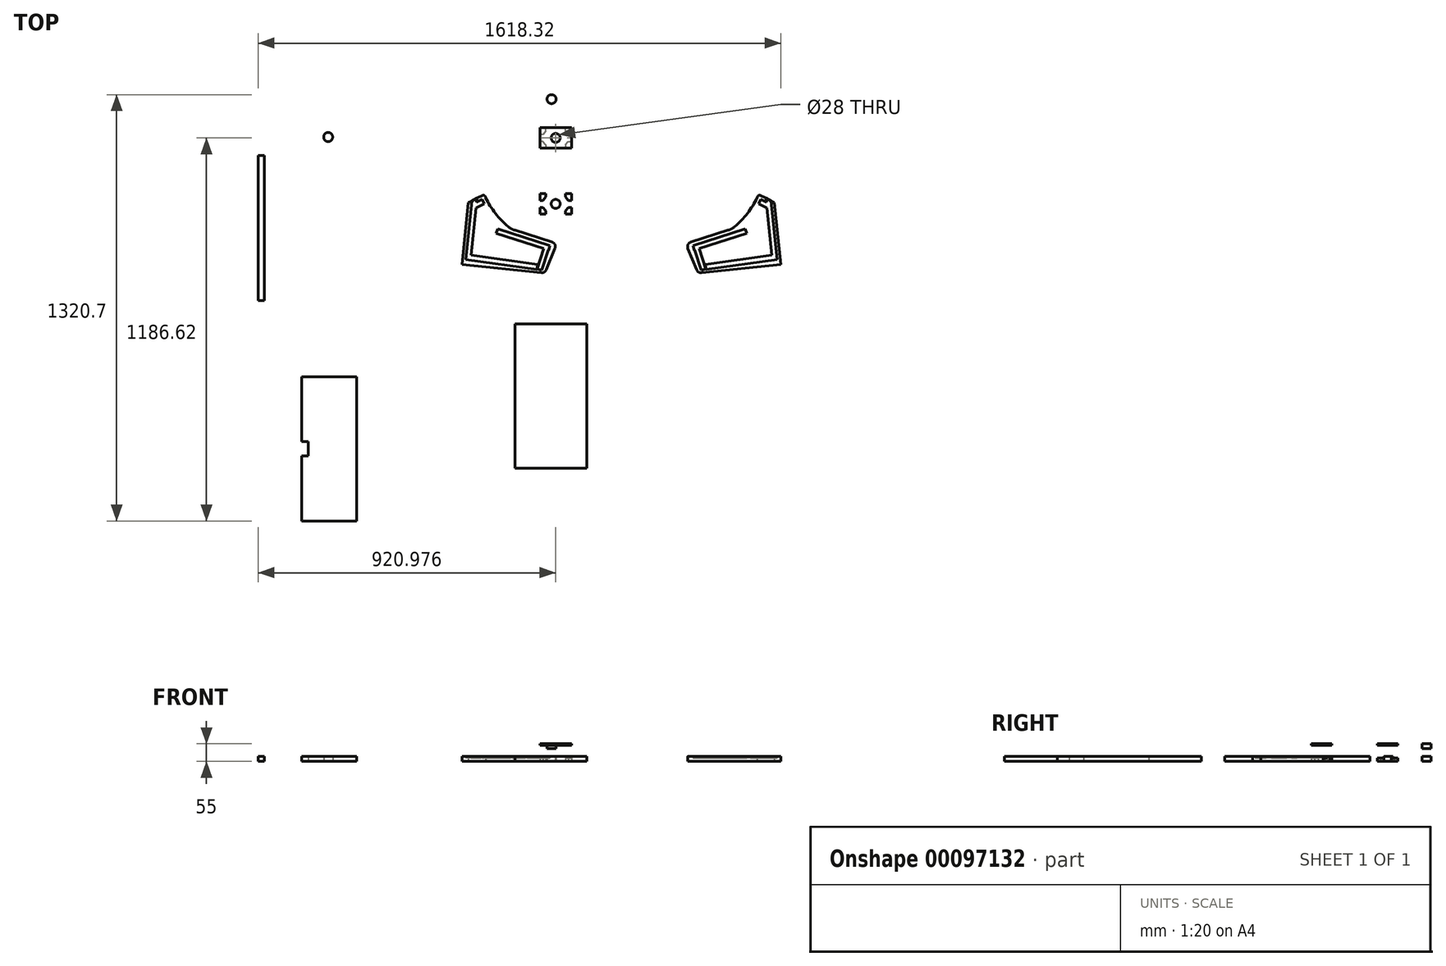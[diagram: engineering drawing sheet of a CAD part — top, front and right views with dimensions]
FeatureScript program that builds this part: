
annotation { "Feature Type Name" : "Feature", "Feature Type Description" : "" }
export const myFeature = defineFeature(function(context is Context, id is Id, definition is map)
    precondition{}
    {
        {
            var Q0;
            Q0=qCreatedBy(makeId("Top.planeOp"),FACE);
            var sketch = newSketch(context, id + "F0", { "sketchPlane" : qUnion([Q0])});
            skCircle(sketch, "E0", {"center": v(416.31, 292.57) * mm, "radius": 14 * mm});
            skCircle(sketch, "E1", {"center": v(380.31, 292.57) * mm, "radius": 14 * mm});
            skCircle(sketch, "E2", {"center": v(389.31, 257.57) * mm, "radius": 14 * mm});
            skCircle(sketch, "E3", {"center": v(425.31, 257.57) * mm, "radius": 14 * mm});
            skCircle(sketch, "E4", {"center": v(407.31, 226.32) * mm, "radius": 14 * mm});
            skCircle(sketch, "E5", {"center": v(443.31, 226.32) * mm, "radius": 14 * mm});
            skCircle(sketch, "E6", {"center": v(416.31, 87.32) * mm, "radius": 14 * mm});
            skCircle(sketch, "E7", {"center": v(380.31, 87.32) * mm, "radius": 14 * mm});
            skCircle(sketch, "E8", {"center": v(389.31, 52.32) * mm, "radius": 14 * mm});
            skCircle(sketch, "E9", {"center": v(425.31, 52.32) * mm, "radius": 14 * mm});
            skCircle(sketch, "E10", {"center": v(407.31, 21.07) * mm, "radius": 14 * mm});
            skCircle(sketch, "E11", {"center": v(443.31, 21.07) * mm, "radius": 14 * mm});
            skCircle(sketch, "E12", {"center": v(428.9, -31.9) * mm, "radius": 14 * mm});
            skLineSegment(sketch, "E13", {"start": v(330.31, -107.92) * mm, "end": v(330.31, 342.08) * mm});
            skLineSegment(sketch, "E14", {"start": v(330.31, 342.08) * mm, "end": v(500.31, 342.08) * mm});
            skLineSegment(sketch, "E15", {"start": v(500.31, -107.92) * mm, "end": v(330.31, -107.92) * mm});
            skLineSegment(sketch, "E16", {"start": v(500.31, -107.92) * mm, "end": v(500.31, 342.08) * mm});
            skArc(sketch, "E17", {"start": v(282.17, -102.25) * mm, "mid": v(291.79, -108.82) * mm, "end": v(302.5, -113.41) * mm});
            skArc(sketch, "E18", {"start": v(212.27, -12.48) * mm, "mid": v(242.43, -61.1) * mm, "end": v(282.17, -102.25) * mm});
            skArc(sketch, "E19", {"start": v(426.9, -169.94) * mm, "mid": v(426.62, -157.9) * mm, "end": v(417.57, -149.94) * mm});
            skLineSegment(sketch, "E20", {"start": v(302.5, -113.41) * mm, "end": v(417.57, -149.94) * mm});
            skArc(sketch, "E21", {"start": v(384.29, -245.32) * mm, "mid": v(393.53, -243.27) * mm, "end": v(399.7, -236.1) * mm});
            skLineSegment(sketch, "E22", {"start": v(426.9, -169.94) * mm, "end": v(399.7, -236.1) * mm});
            skLineSegment(sketch, "E23", {"start": v(384.29, -245.32) * mm, "end": v(138.88, -219.86) * mm});
            skLineSegment(sketch, "E24", {"start": v(386.04, -237.9) * mm, "end": v(371.77, -233.27) * mm});
            skLineSegment(sketch, "E25", {"start": v(371.77, -233.27) * mm, "end": v(392.17, -170.5) * mm});
            skLineSegment(sketch, "E26", {"start": v(392.17, -170.5) * mm, "end": v(406.43, -175.14) * mm});
            skLineSegment(sketch, "E27", {"start": v(406.43, -175.14) * mm, "end": v(386.04, -237.9) * mm});
            skLineSegment(sketch, "E28", {"start": v(244.88, -122.79) * mm, "end": v(249.52, -108.52) * mm});
            skLineSegment(sketch, "E29", {"start": v(249.52, -108.52) * mm, "end": v(411.2, -161.05) * mm});
            skLineSegment(sketch, "E30", {"start": v(411.2, -161.05) * mm, "end": v(406.56, -175.32) * mm});
            skLineSegment(sketch, "E31", {"start": v(406.56, -175.32) * mm, "end": v(244.88, -122.79) * mm});
            skCircle(sketch, "E32", {"center": v(-275.31, 175.36) * mm, "radius": 14 * mm});
            skCircle(sketch, "E33", {"center": v(-99.31, 175.05) * mm, "radius": 14 * mm});
            skLineSegment(sketch, "E34", {"start": v(-500.31, 141.57) * mm, "end": v(-50.31, 141.57) * mm});
            skLineSegment(sketch, "E35", {"start": v(-50.31, 141.57) * mm, "end": v(-50.31, 207.57) * mm});
            skLineSegment(sketch, "E36", {"start": v(-50.31, 207.57) * mm, "end": v(-500.31, 207.57) * mm});
            skLineSegment(sketch, "E37", {"start": v(-500.31, 207.57) * mm, "end": v(-500.31, 141.57) * mm});
            skLineSegment(sketch, "E38", {"start": v(372.72, -219.9) * mm, "end": v(370.63, -234.76) * mm});
            skLineSegment(sketch, "E39", {"start": v(370.63, -234.76) * mm, "end": v(150.6, -203.84) * mm});
            skArc(sketch, "E40", {"start": v(-372.38, 189.04) * mm, "mid": v(-361.31, 175.39) * mm, "end": v(-372.31, 161.68) * mm});
            skArc(sketch, "E41", {"start": v(-372.31, 161.68) * mm, "mid": v(-375.31, 158.67) * mm, "end": v(-378.31, 161.68) * mm});
            skArc(sketch, "E42", {"start": v(-378.31, 161.68) * mm, "mid": v(-389.31, 175.39) * mm, "end": v(-378.25, 189.04) * mm});
            skArc(sketch, "E43", {"start": v(-378.25, 189.04) * mm, "mid": v(-375.31, 191.43) * mm, "end": v(-372.38, 189.04) * mm});
            skArc(sketch, "E44", {"start": v(-172.38, 189.04) * mm, "mid": v(-161.31, 175.39) * mm, "end": v(-172.31, 161.68) * mm});
            skArc(sketch, "E45", {"start": v(-172.31, 161.68) * mm, "mid": v(-175.31, 158.67) * mm, "end": v(-178.31, 161.68) * mm});
            skArc(sketch, "E46", {"start": v(-178.31, 161.68) * mm, "mid": v(-189.31, 175.39) * mm, "end": v(-178.25, 189.04) * mm});
            skArc(sketch, "E47", {"start": v(-178.25, 189.04) * mm, "mid": v(-175.31, 191.43) * mm, "end": v(-172.38, 189.04) * mm});
            skCircle(sketch, "E48", {"center": v(-455.31, 172.67) * mm, "radius": 14 * mm});
            skLineSegment(sketch, "E49", {"start": v(632.56, -327.89) * mm, "end": v(632.56, 378.8) * mm, "construction": true});
            skLineSegment(sketch, "E50.MirrorCS", {"start": v(-357.1, -1014.12) * mm, "end": v(-357.1, -813.12) * mm});
            skLineSegment(sketch, "E51", {"start": v(-357.1, -567.12) * mm, "end": v(-187.1, -567.12) * mm});
            skLineSegment(sketch, "E52", {"start": v(-187.1, -567.12) * mm, "end": v(-187.1, -1014.12) * mm});
            skLineSegment(sketch, "E53", {"start": v(-187.1, -1014.12) * mm, "end": v(-357.1, -1014.12) * mm});
            skLineSegment(sketch, "E54.bottom", {"start": v(302.99, -403.6) * mm, "end": v(525.17, -403.6) * mm});
            skLineSegment(sketch, "E54.top", {"start": v(302.99, -850.6) * mm, "end": v(525.17, -850.6) * mm});
            skLineSegment(sketch, "E54.left", {"start": v(302.99, -403.6) * mm, "end": v(302.99, -850.6) * mm});
            skLineSegment(sketch, "E54.right", {"start": v(525.17, -403.6) * mm, "end": v(525.17, -850.6) * mm});
            skLineSegment(sketch, "E55.bottom", {"start": v(379.9, -63.4) * mm, "end": v(477.9, -63.4) * mm});
            skLineSegment(sketch, "E55.top", {"start": v(379.9, -0.4) * mm, "end": v(477.9, -0.4) * mm});
            skLineSegment(sketch, "E55.left", {"start": v(379.9, -63.4) * mm, "end": v(379.9, -0.4) * mm});
            skLineSegment(sketch, "E55.right", {"start": v(477.9, -63.4) * mm, "end": v(477.9, -0.4) * mm});
            skLineSegment(sketch, "E56.bottom", {"start": v(379.9, 204) * mm, "end": v(477.9, 204) * mm});
            skLineSegment(sketch, "E56.top", {"start": v(379.9, 141) * mm, "end": v(477.9, 141) * mm});
            skLineSegment(sketch, "E56.left", {"start": v(379.9, 204) * mm, "end": v(379.9, 141) * mm});
            skLineSegment(sketch, "E56.right", {"start": v(477.9, 204) * mm, "end": v(477.9, 141) * mm});
            skPoint(sketch, "E56.middle", {"position": v(428.9, 172.5) * mm});
            skLineSegment(sketch, "E57", {"start": v(477.9, -0.4) * mm, "end": v(477.9, 141) * mm, "construction": true});
            skLineSegment(sketch, "E58", {"start": v(477.9, 70.3) * mm, "end": v(336.42, 70.3) * mm, "construction": true});
            skLineSegment(sketch, "E59", {"start": v(398.9, -63.4) * mm, "end": v(398.9, -42.9) * mm, "construction": true});
            skLineSegment(sketch, "E60", {"start": v(428.9, -63.4) * mm, "end": v(428.9, 0) * mm, "construction": true});
            skLineSegment(sketch, "E61", {"start": v(379.9, -31.9) * mm, "end": v(477.9, -31.9) * mm, "construction": true});
            skLineSegment(sketch, "E62.0", {"start": v(379.9, -20.9) * mm, "end": v(398.9, -20.9) * mm, "construction": true});
            skLineSegment(sketch, "E63.MirrorCS", {"start": v(379.9, -42.9) * mm, "end": v(398.9, -42.9) * mm, "construction": true});
            skLineSegment(sketch, "E64.MirrorCS", {"start": v(458.9, -63.4) * mm, "end": v(458.9, -42.9) * mm, "construction": true});
            skLineSegment(sketch, "E65.trimOffspring", {"start": v(420.24, -42.9) * mm, "end": v(437.56, -42.9) * mm, "construction": true});
            skLineSegment(sketch, "E66.trimOffspring", {"start": v(398.9, -20.9) * mm, "end": v(398.9, 0) * mm, "construction": true});
            skLineSegment(sketch, "E67.trimOffspring", {"start": v(420.24, -20.9) * mm, "end": v(437.56, -20.9) * mm, "construction": true});
            skLineSegment(sketch, "E68.trimOffspring", {"start": v(458.9, -20.9) * mm, "end": v(477.9, -20.9) * mm, "construction": true});
            skLineSegment(sketch, "E69.trimOffspring", {"start": v(458.9, -20.9) * mm, "end": v(458.9, 0) * mm, "construction": true});
            skLineSegment(sketch, "E70.trimOffspring", {"start": v(458.9, -42.9) * mm, "end": v(477.9, -42.9) * mm, "construction": true});
            skLineSegment(sketch, "E71", {"start": v(398.9, -53.15) * mm, "end": v(389.4, -42.9) * mm});
            skLineSegment(sketch, "E72", {"start": v(389.4, -42.9) * mm, "end": v(379.9, -42.9) * mm});
            skLineSegment(sketch, "E73", {"start": v(398.9, -53.15) * mm, "end": v(398.9, -63.4) * mm});
            skLineSegment(sketch, "E74.MirrorCS", {"start": v(389.4, -20.9) * mm, "end": v(379.9, -20.9) * mm});
            skLineSegment(sketch, "E75.MirrorCS", {"start": v(398.9, -10.65) * mm, "end": v(389.4, -20.9) * mm});
            skLineSegment(sketch, "E76.MirrorCS", {"start": v(398.9, -10.65) * mm, "end": v(398.9, -0.4) * mm});
            skLineSegment(sketch, "E77.MirrorCS", {"start": v(458.9, -10.65) * mm, "end": v(468.4, -20.9) * mm});
            skLineSegment(sketch, "E78.MirrorCS", {"start": v(458.9, -10.65) * mm, "end": v(458.9, -0.4) * mm});
            skLineSegment(sketch, "E79.MirrorCS", {"start": v(468.4, -20.9) * mm, "end": v(477.9, -20.9) * mm});
            skLineSegment(sketch, "E80.MirrorCS", {"start": v(468.4, -42.9) * mm, "end": v(477.9, -42.9) * mm});
            skLineSegment(sketch, "E81.MirrorCS", {"start": v(458.9, -53.15) * mm, "end": v(468.4, -42.9) * mm});
            skLineSegment(sketch, "E82.MirrorCS", {"start": v(458.9, -53.15) * mm, "end": v(458.9, -63.4) * mm});
            skLineSegment(sketch, "E83.MirrorCS", {"start": v(398.9, 161.5) * mm, "end": v(398.9, 140.6) * mm, "construction": true});
            skLineSegment(sketch, "E84.MirrorCS", {"start": v(398.9, 151.25) * mm, "end": v(389.4, 161.5) * mm});
            skLineSegment(sketch, "E85.MirrorCS", {"start": v(379.9, 161.5) * mm, "end": v(398.9, 161.5) * mm, "construction": true});
            skLineSegment(sketch, "E86.MirrorCS", {"start": v(458.9, 193.75) * mm, "end": v(468.4, 183.5) * mm});
            skLineSegment(sketch, "E87.MirrorCS", {"start": v(458.9, 193.75) * mm, "end": v(458.9, 204) * mm});
            skLineSegment(sketch, "E88.MirrorCS", {"start": v(458.9, 161.5) * mm, "end": v(477.9, 161.5) * mm, "construction": true});
            skLineSegment(sketch, "E89.MirrorCS", {"start": v(458.9, 183.5) * mm, "end": v(477.9, 183.5) * mm, "construction": true});
            skLineSegment(sketch, "E90.MirrorCS", {"start": v(398.9, 204) * mm, "end": v(398.9, 183.5) * mm, "construction": true});
            skLineSegment(sketch, "E91.MirrorCS", {"start": v(398.9, 193.75) * mm, "end": v(398.9, 204) * mm});
            skLineSegment(sketch, "E92.MirrorCS", {"start": v(458.9, 161.5) * mm, "end": v(458.9, 140.6) * mm, "construction": true});
            skLineSegment(sketch, "E93.MirrorCS", {"start": v(398.9, 151.25) * mm, "end": v(398.9, 141) * mm});
            skLineSegment(sketch, "E94.MirrorCS", {"start": v(468.4, 183.5) * mm, "end": v(477.9, 183.5) * mm});
            skLineSegment(sketch, "E95.MirrorCS", {"start": v(458.9, 204) * mm, "end": v(458.9, 183.5) * mm, "construction": true});
            skLineSegment(sketch, "E96.MirrorCS", {"start": v(420.24, 183.5) * mm, "end": v(437.56, 183.5) * mm, "construction": true});
            skLineSegment(sketch, "E97.MirrorCS", {"start": v(389.4, 183.5) * mm, "end": v(379.9, 183.5) * mm});
            skLineSegment(sketch, "E98.MirrorCS", {"start": v(389.4, 161.5) * mm, "end": v(379.9, 161.5) * mm});
            skLineSegment(sketch, "E99.MirrorCS", {"start": v(379.9, 183.5) * mm, "end": v(398.9, 183.5) * mm, "construction": true});
            skLineSegment(sketch, "E100.MirrorCS", {"start": v(468.4, 161.5) * mm, "end": v(477.9, 161.5) * mm});
            skLineSegment(sketch, "E101.MirrorCS", {"start": v(420.24, 161.5) * mm, "end": v(437.56, 161.5) * mm, "construction": true});
            skLineSegment(sketch, "E102.MirrorCS", {"start": v(458.9, 151.25) * mm, "end": v(458.9, 141) * mm});
            skLineSegment(sketch, "E103.MirrorCS", {"start": v(398.9, 193.75) * mm, "end": v(389.4, 183.5) * mm});
            skLineSegment(sketch, "E104.MirrorCS", {"start": v(458.9, 151.25) * mm, "end": v(468.4, 161.5) * mm});
            skLineSegment(sketch, "E105.MirrorCS", {"start": v(379.9, 172.5) * mm, "end": v(477.9, 172.5) * mm, "construction": true});
            skLineSegment(sketch, "E106.MirrorCS", {"start": v(428.9, 204) * mm, "end": v(428.9, 140.6) * mm, "construction": true});
            skCircle(sketch, "E107.MirrorC", {"center": v(428.9, 172.5) * mm, "radius": 14 * mm});
            skLineSegment(sketch, "E108.bottom", {"start": v(-492.08, 118) * mm, "end": v(-473.48, 118) * mm});
            skLineSegment(sketch, "E108.top", {"start": v(-492.08, -332) * mm, "end": v(-473.48, -332) * mm});
            skLineSegment(sketch, "E108.left", {"start": v(-492.08, 118) * mm, "end": v(-492.08, -332) * mm});
            skLineSegment(sketch, "E108.right", {"start": v(-473.48, 118) * mm, "end": v(-473.48, -332) * mm});
            skLineSegment(sketch, "E109.0", {"start": v(212.38, -12.43) * mm, "end": v(212.27, -12.48) * mm});
            skLineSegment(sketch, "E110.0", {"start": v(203.5, -5.64) * mm, "end": v(158.85, -27.41) * mm});
            skLineSegment(sketch, "E111", {"start": v(212.38, -12.43) * mm, "end": v(210.18, -7.94) * mm});
            skPoint(sketch, "E112.visualSharp", {"position": v(208, -3.45) * mm});
            skArc(sketch, "E112.filletArc", {"start": v(210.18, -7.94) * mm, "mid": v(207.32, -5.4) * mm, "end": v(203.5, -5.64) * mm});
            skLineSegment(sketch, "E113", {"start": v(201.09, -17.94) * mm, "end": v(207.66, -31.42) * mm});
            skLineSegment(sketch, "E114", {"start": v(158.85, -27.41) * mm, "end": v(138.88, -219.86) * mm});
            skLineSegment(sketch, "E115.0", {"start": v(169.44, -22.25) * mm, "end": v(150.6, -203.84) * mm});
            skLineSegment(sketch, "E116.0", {"start": v(185.32, -14.5) * mm, "end": v(165.46, -205.93) * mm});
            skLineSegment(sketch, "E117.trimOffspring", {"start": v(201.09, -17.94) * mm, "end": v(184.1, -26.22) * mm});
            skLineSegment(sketch, "E118.trimOffspring", {"start": v(167, -191) * mm, "end": v(372.72, -219.9) * mm});
            skLineSegment(sketch, "E119", {"start": v(207.66, -31.42) * mm, "end": v(182.28, -43.8) * mm});
            skPoint(sketch, "E120.end.orphan", {"position": v(42.5, -173.5) * mm});
            skLineSegment(sketch, "E121.MirrorCS", {"start": v(1052.74, -12.43) * mm, "end": v(1052.84, -12.48) * mm});
            skLineSegment(sketch, "E122.MirrorCS", {"start": v(1052.74, -12.43) * mm, "end": v(1054.93, -7.94) * mm});
            skLineSegment(sketch, "E123.MirrorCS", {"start": v(1064.03, -17.94) * mm, "end": v(1057.45, -31.42) * mm});
            skArc(sketch, "E124.MirrorCS", {"start": v(1054.93, -7.94) * mm, "mid": v(1057.8, -5.4) * mm, "end": v(1061.62, -5.64) * mm});
            skLineSegment(sketch, "E125.MirrorCS", {"start": v(1057.45, -31.42) * mm, "end": v(1082.84, -43.8) * mm});
            skLineSegment(sketch, "E126.MirrorCS", {"start": v(1064.03, -17.94) * mm, "end": v(1081.01, -26.22) * mm});
            skArc(sketch, "E127.MirrorCS", {"start": v(838.21, -169.94) * mm, "mid": v(838.5, -157.9) * mm, "end": v(847.55, -149.94) * mm});
            skLineSegment(sketch, "E128.MirrorCS", {"start": v(872.95, -170.5) * mm, "end": v(858.69, -175.14) * mm});
            skLineSegment(sketch, "E129.MirrorCS", {"start": v(853.92, -161.05) * mm, "end": v(858.56, -175.32) * mm});
            skLineSegment(sketch, "E130.MirrorCS", {"start": v(879.08, -237.9) * mm, "end": v(893.35, -233.27) * mm});
            skLineSegment(sketch, "E131.MirrorCS", {"start": v(858.69, -175.14) * mm, "end": v(879.08, -237.9) * mm});
            skLineSegment(sketch, "E132.MirrorCS", {"start": v(892.4, -219.9) * mm, "end": v(894.49, -234.76) * mm});
            skLineSegment(sketch, "E133.MirrorCS", {"start": v(838.21, -169.94) * mm, "end": v(865.41, -236.1) * mm});
            skArc(sketch, "E134.MirrorCS", {"start": v(880.83, -245.32) * mm, "mid": v(871.59, -243.27) * mm, "end": v(865.41, -236.1) * mm});
            skLineSegment(sketch, "E135.MirrorCS", {"start": v(893.35, -233.27) * mm, "end": v(872.95, -170.5) * mm});
            skLineSegment(sketch, "E136.MirrorCS", {"start": v(1061.62, -5.64) * mm, "end": v(1106.27, -27.41) * mm});
            skLineSegment(sketch, "E137.MirrorCS", {"start": v(1015.6, -108.52) * mm, "end": v(853.92, -161.05) * mm});
            skLineSegment(sketch, "E138.MirrorCS", {"start": v(1020.24, -122.79) * mm, "end": v(1015.6, -108.52) * mm});
            skLineSegment(sketch, "E139.MirrorCS", {"start": v(962.61, -113.41) * mm, "end": v(847.55, -149.94) * mm});
            skArc(sketch, "E140.MirrorCS", {"start": v(1052.84, -12.48) * mm, "mid": v(1022.7, -61.1) * mm, "end": v(982.95, -102.25) * mm});
            skArc(sketch, "E141.MirrorCS", {"start": v(982.95, -102.25) * mm, "mid": v(973.33, -108.82) * mm, "end": v(962.61, -113.41) * mm});
            skPoint(sketch, "E142.MirrorP", {"position": v(1222.62, -173.5) * mm});
            skLineSegment(sketch, "E143.MirrorCS", {"start": v(894.49, -234.76) * mm, "end": v(1114.52, -203.84) * mm});
            skLineSegment(sketch, "E144.MirrorCS", {"start": v(1079.8, -14.5) * mm, "end": v(1099.66, -205.93) * mm});
            skLineSegment(sketch, "E145.MirrorCS", {"start": v(1095.68, -22.25) * mm, "end": v(1114.52, -203.84) * mm});
            skLineSegment(sketch, "E146.MirrorCS", {"start": v(1106.27, -27.41) * mm, "end": v(1126.24, -219.86) * mm});
            skLineSegment(sketch, "E147.MirrorCS", {"start": v(880.83, -245.32) * mm, "end": v(1126.24, -219.86) * mm});
            skPoint(sketch, "E148.MirrorP", {"position": v(1057.13, -3.45) * mm});
            skLineSegment(sketch, "E149.MirrorCS", {"start": v(1098.1, -191) * mm, "end": v(892.4, -219.9) * mm});
            skLineSegment(sketch, "E150.MirrorCS", {"start": v(858.56, -175.32) * mm, "end": v(1020.24, -122.79) * mm});
            skLineSegment(sketch, "E151.bottom", {"start": v(-337.1, -768.12) * mm, "end": v(-357.1, -768.12) * mm});
            skLineSegment(sketch, "E151.top", {"start": v(-337.1, -813.12) * mm, "end": v(-357.1, -813.12) * mm});
            skLineSegment(sketch, "E151.left", {"start": v(-337.1, -768.12) * mm, "end": v(-337.1, -813.12) * mm});
            skPoint(sketch, "E151.middle", {"position": v(-357.1, -790.62) * mm});
            skPoint(sketch, "E152.orphan", {"position": v(-377.1, -813.12) * mm});
            skLineSegment(sketch, "E153.trimOffspring", {"start": v(-357.1, -768.12) * mm, "end": v(-357.1, -567.12) * mm});
            skPoint(sketch, "E154.orphan", {"position": v(-377.1, -768.12) * mm});
            skSolve(sketch);
        }
        {
            var Q0;
            Q0=makeQuery(id+"F0.imprint","IMPRINT",FACE,{"disambiguationData":[TD([[makeQuery(id+"F0.imprint","IMPRINT",EDGE,{"derivedFrom":sQuery(id+"F0.wireOp",EDGE,"212e7dfc-0aa7-45bf-9c8c-43930fb3721e")}),1.0]])]});
            var Q1;
            Q1=makeQuery(id+"F0.imprint","IMPRINT",FACE,{"disambiguationData":[TD([[makeQuery(id+"F0.imprint","IMPRINT",EDGE,{"derivedFrom":sQuery(id+"F0.wireOp",EDGE,"3e686249-5a05-4be7-8b18-40a04c8c0b60")}),1.0]])]});
            var Q2;
            Q2=makeQuery(id+"F0.imprint","IMPRINT",FACE,{"disambiguationData":[TD([[makeQuery(id+"F0.imprint","IMPRINT",EDGE,{"derivedFrom":sQuery(id+"F0.wireOp",EDGE,"E32")}),1.0]])]});
            var Q3;
            Q3=makeQuery(id+"F0.imprint","IMPRINT",FACE,{"disambiguationData":[TD([[makeQuery(id+"F0.imprint","IMPRINT",EDGE,{"derivedFrom":sQuery(id+"F0.wireOp",EDGE,"6e44e23a-00e6-4dfd-9480-57aab4792efb0.MirrorCS")}),-1.0]])]});
            var Q4;
            Q4=makeQuery(id+"F0.imprint","IMPRINT",FACE,{"disambiguationData":[TD([[makeQuery(id+"F0.imprint","IMPRINT",EDGE,{"derivedFrom":sQuery(id+"F0.wireOp",EDGE,"E54.bottom")}),-1.0]])]});
            var Q5;
            Q5=makeQuery(id+"F0.imprint","IMPRINT",FACE,{"disambiguationData":[TD([[makeQuery(id+"F0.imprint","IMPRINT",EDGE,{"derivedFrom":sQuery(id+"F0.wireOp",EDGE,"E108.bottom")}),-1.0]])]});
            var Q6;
            Q6=makeQuery(id+"F0.imprint","IMPRINT",FACE,{"disambiguationData":[TD([[makeQuery(id+"F0.imprint","IMPRINT",EDGE,{"derivedFrom":sQuery(id+"F0.wireOp",EDGE,"dx2RWpmp-VK7X-Jnnr-GJcX-QQeztWBlGX27.bottom")}),1.0]])]});
            var Q7;
            Q7=makeQuery(id+"F0.imprint","IMPRINT",FACE,{"disambiguationData":[TD([[makeQuery(id+"F0.imprint","IMPRINT",EDGE,{"derivedFrom":sQuery(id+"F0.wireOp",EDGE,"E50.MirrorCS")}),-1.0]])]});
            var Q8;
            Q8=makeQuery(id+"F0.imprint","IMPRINT",FACE,{"disambiguationData":[TD([[makeQuery(id+"F0.imprint","IMPRINT",EDGE,{"derivedFrom":sQuery(id+"F0.wireOp",EDGE,"E0")}),1.0]])]});
            var Q9;
            Q9=makeQuery(id+"F0.imprint","IMPRINT",FACE,{"disambiguationData":[TD([[makeQuery(id+"F0.imprint","IMPRINT",EDGE,{"derivedFrom":sQuery(id+"F0.wireOp",EDGE,"E17")}),-1.0]])]});
            var Q10;
            Q10=makeQuery(id+"F0.imprint","IMPRINT",FACE,{"disambiguationData":[TD([[makeQuery(id+"F0.imprint","IMPRINT",EDGE,{"derivedFrom":sQuery(id+"F0.wireOp",EDGE,"E121.MirrorCS")}),1.0]])]});
            extrude(context, id + "F1", {"entities" : qUnion([Q0, Q1, Q2, Q3, Q4, Q5, Q6, Q7, Q8, Q9, Q10]), "depth" : 15 * mm});
        }
        {
            var Q0;
            Q0=makeQuery(id+"F0.imprint","IMPRINT",FACE,{"disambiguationData":[TD([[makeQuery(id+"F0.imprint","IMPRINT",EDGE,{"derivedFrom":sQuery(id+"F0.wireOp",EDGE,"6a3160c0-6564-4787-b3fb-6f14df5ae7cb")}),-1.0]])]});
            var Q1;
            Q1=makeQuery(id+"F0.imprint","IMPRINT",FACE,{"disambiguationData":[TD([[makeQuery(id+"F0.imprint","IMPRINT",EDGE,{"derivedFrom":sQuery(id+"F0.wireOp",EDGE,"13f106b7-fe38-453e-a0d0-f60d13468fab")}),-1.0]])]});
            var Q2;
            Q2=makeQuery(id+"F0.imprint","IMPRINT",FACE,{"disambiguationData":[TD([[makeQuery(id+"F0.imprint","IMPRINT",EDGE,{"derivedFrom":sQuery(id+"F0.wireOp",EDGE,"0d5a4450-49e4-4b3d-a1dc-0e6f84640f1e")}),-1.0]])]});
            var Q3;
            {var subQ2=sQuery(id+"F0.wireOp",EDGE,"E26");Q3=makeQuery(id+"F0.imprint","IMPRINT",FACE,{"disambiguationData":[TD([[makeQuery(id+"F0.imprint","IMPRINT",EDGE,{"derivedFrom":subQ2}),1.0]])]});}
            var Q4;
            Q4=makeQuery(id+"F0.imprint","IMPRINT",FACE,{"disambiguationData":[TD([[makeQuery(id+"F0.imprint","IMPRINT",EDGE,{"derivedFrom":sQuery(id+"F0.wireOp",EDGE,"E120")}),-1.0]])]});
            var Q5;
            {var subQ1=sQuery(id+"F0.wireOp",EDGE,"d7afa14e-a9a5-498d-b6fe-0a06bc60c3a90.MirrorCS");Q5=makeQuery(id+"F0.imprint","IMPRINT",FACE,{"disambiguationData":[TD([[makeQuery(id+"F0.imprint","IMPRINT",EDGE,{"derivedFrom":subQ1}),-1.0]])]});}
            var Q6;
            Q6=makeQuery(id+"F0.imprint","IMPRINT",FACE,{"disambiguationData":[TD([[makeQuery(id+"F0.imprint","IMPRINT",EDGE,{"derivedFrom":sQuery(id+"F0.wireOp",EDGE,"6e44e23a-00e6-4dfd-9480-57aab4792efb8.MirrorCS")}),1.0]])]});
            var Q7;
            Q7=makeQuery(id+"F0.imprint","IMPRINT",FACE,{"disambiguationData":[TD([[makeQuery(id+"F0.imprint","IMPRINT",EDGE,{"derivedFrom":sQuery(id+"F0.wireOp",EDGE,"6e44e23a-00e6-4dfd-9480-57aab4792efb4.MirrorCS")}),1.0]])]});
            var Q8;
            Q8=makeQuery(id+"F0.imprint","IMPRINT",FACE,{"disambiguationData":[TD([[makeQuery(id+"F0.imprint","IMPRINT",EDGE,{"derivedFrom":sQuery(id+"F0.wireOp",EDGE,"6e44e23a-00e6-4dfd-9480-57aab4792efb3.MirrorCS")}),1.0]])]});
            var Q9;
            Q9=makeQuery(id+"F0.imprint","IMPRINT",FACE,{"disambiguationData":[TD([[makeQuery(id+"F0.imprint","IMPRINT",EDGE,{"derivedFrom":sQuery(id+"F0.wireOp",EDGE,"6e44e23a-00e6-4dfd-9480-57aab4792efb5.MirrorCS")}),1.0]])]});
            var Q10;
            {var subQ0=sQuery(id+"F0.wireOp",EDGE,"E74.MirrorCS");Q10=makeQuery(id+"F0.imprint","IMPRINT",FACE,{"disambiguationData":[TD([[makeQuery(id+"F0.imprint","IMPRINT",EDGE,{"derivedFrom":subQ0}),-1.0]])]});}
            var Q11;
            Q11=makeQuery(id+"F0.imprint","IMPRINT",FACE,{"disambiguationData":[TD([[makeQuery(id+"F0.imprint","IMPRINT",EDGE,{"derivedFrom":sQuery(id+"F0.wireOp",EDGE,"E77.MirrorCS")}),1.0]])]});
            var Q12;
            Q12=makeQuery(id+"F0.imprint","IMPRINT",FACE,{"disambiguationData":[TD([[makeQuery(id+"F0.imprint","IMPRINT",EDGE,{"derivedFrom":sQuery(id+"F0.wireOp",EDGE,"E71")}),1.0]])]});
            var Q13;
            {var subQ3=sQuery(id+"F0.wireOp",EDGE,"E80.MirrorCS");Q13=makeQuery(id+"F0.imprint","IMPRINT",FACE,{"disambiguationData":[TD([[makeQuery(id+"F0.imprint","IMPRINT",EDGE,{"derivedFrom":subQ3}),-1.0]])]});}
            var Q14;
            {var subQ0=sQuery(id+"F0.wireOp",EDGE,"E91.MirrorCS");Q14=makeQuery(id+"F0.imprint","IMPRINT",FACE,{"disambiguationData":[TD([[makeQuery(id+"F0.imprint","IMPRINT",EDGE,{"derivedFrom":subQ0}),1.0]])]});}
            var Q15;
            Q15=makeQuery(id+"F0.imprint","IMPRINT",FACE,{"disambiguationData":[TD([[makeQuery(id+"F0.imprint","IMPRINT",EDGE,{"derivedFrom":sQuery(id+"F0.wireOp",EDGE,"E86.MirrorCS")}),1.0]])]});
            var Q16;
            Q16=makeQuery(id+"F0.imprint","IMPRINT",FACE,{"disambiguationData":[TD([[makeQuery(id+"F0.imprint","IMPRINT",EDGE,{"derivedFrom":sQuery(id+"F0.wireOp",EDGE,"E84.MirrorCS")}),1.0]])]});
            var Q17;
            {var subQ0=sQuery(id+"F0.wireOp",EDGE,"E100.MirrorCS");Q17=makeQuery(id+"F0.imprint","IMPRINT",FACE,{"disambiguationData":[TD([[makeQuery(id+"F0.imprint","IMPRINT",EDGE,{"derivedFrom":subQ0}),-1.0]])]});}
            var Q18;
            {var subQ0=sQuery(id+"F0.wireOp",EDGE,"E24");Q18=makeQuery(id+"F0.imprint","IMPRINT",FACE,{"disambiguationData":[TD([[makeQuery(id+"F0.imprint","IMPRINT",EDGE,{"derivedFrom":subQ0}),-1.0]])]});}
            var Q19;
            {var subQ0=sQuery(id+"F0.wireOp",EDGE,"d7afa14e-a9a5-498d-b6fe-0a06bc60c3a90.MirrorCS");Q19=makeQuery(id+"F0.imprint","IMPRINT",FACE,{"disambiguationData":[TD([[makeQuery(id+"F0.imprint","IMPRINT",EDGE,{"derivedFrom":subQ0}),1.0]])]});}
            var Q20;
            {var subQ0=sQuery(id+"F0.wireOp",EDGE,"d7afa14e-a9a5-498d-b6fe-0a06bc60c3a94.MirrorCS");Q20=makeQuery(id+"F0.imprint","IMPRINT",FACE,{"disambiguationData":[TD([[makeQuery(id+"F0.imprint","IMPRINT",EDGE,{"derivedFrom":subQ0}),1.0]])]});}
            var Q21;
            {var subQ4=sQuery(id+"F0.wireOp",EDGE,"E115.0");Q21=makeQuery(id+"F0.imprint","IMPRINT",FACE,{"disambiguationData":[TD([[makeQuery(id+"F0.imprint","IMPRINT",EDGE,{"derivedFrom":subQ4}),1.0]])]});}
            var Q22;
            Q22=makeQuery(id+"F0.imprint","IMPRINT",FACE,{"disambiguationData":[TD([[makeQuery(id+"F0.imprint","IMPRINT",EDGE,{"derivedFrom":sQuery(id+"F0.wireOp",EDGE,"E113")}),-1.0]])]});
            var Q23;
            {var subQ0=sQuery(id+"F0.wireOp",EDGE,"E38");Q23=makeQuery(id+"F0.imprint","IMPRINT",FACE,{"disambiguationData":[TD([[makeQuery(id+"F0.imprint","IMPRINT",EDGE,{"derivedFrom":subQ0}),-1.0]])]});}
            var Q24;
            {var subQ5=sQuery(id+"F0.wireOp",EDGE,"E145.MirrorCS");Q24=makeQuery(id+"F0.imprint","IMPRINT",FACE,{"disambiguationData":[TD([[makeQuery(id+"F0.imprint","IMPRINT",EDGE,{"derivedFrom":subQ5}),-1.0]])]});}
            var Q25;
            {var subQ0=sQuery(id+"F0.wireOp",EDGE,"E132.MirrorCS");Q25=makeQuery(id+"F0.imprint","IMPRINT",FACE,{"disambiguationData":[TD([[makeQuery(id+"F0.imprint","IMPRINT",EDGE,{"derivedFrom":subQ0}),1.0]])]});}
            var Q26;
            {var subQ0=sQuery(id+"F0.wireOp",EDGE,"E130.MirrorCS");Q26=makeQuery(id+"F0.imprint","IMPRINT",FACE,{"disambiguationData":[TD([[makeQuery(id+"F0.imprint","IMPRINT",EDGE,{"derivedFrom":subQ0}),1.0]])]});}
            var Q27;
            {var subQ1=sQuery(id+"F0.wireOp",EDGE,"E128.MirrorCS");Q27=makeQuery(id+"F0.imprint","IMPRINT",FACE,{"disambiguationData":[TD([[makeQuery(id+"F0.imprint","IMPRINT",EDGE,{"derivedFrom":subQ1}),-1.0]])]});}
            var Q28;
            {var subQ0=sQuery(id+"F0.wireOp",EDGE,"E128.MirrorCS");Q28=makeQuery(id+"F0.imprint","IMPRINT",FACE,{"disambiguationData":[TD([[makeQuery(id+"F0.imprint","IMPRINT",EDGE,{"derivedFrom":subQ0}),1.0]])]});}
            var Q29;
            Q29=makeQuery(id+"F0.imprint","IMPRINT",FACE,{"disambiguationData":[TD([[makeQuery(id+"F0.imprint","IMPRINT",EDGE,{"derivedFrom":sQuery(id+"F0.wireOp",EDGE,"E123.MirrorCS")}),1.0]])]});
            var Q30;
            {var subQ0=sQuery(id+"F0.wireOp",EDGE,"E26");Q30=makeQuery(id+"F0.imprint","IMPRINT",FACE,{"disambiguationData":[TD([[makeQuery(id+"F0.imprint","IMPRINT",EDGE,{"derivedFrom":subQ0}),-1.0]])]});}
            extrude(context, id + "F2", {"entities" : qUnion([Q0, Q1, Q2, Q3, Q4, Q5, Q6, Q7, Q8, Q9, Q10, Q11, Q12, Q13, Q14, Q15, Q16, Q17, Q18, Q19, Q20, Q21, Q22, Q23, Q24, Q25, Q26, Q27, Q28, Q29, Q30]), "operationType" : NewBodyOperationType.ADD, "depth" : 10 * mm});
        }
        {
            var Q0;
            Q0=makeQuery(id+"F2.opExtrude","CAP_FACE",FACE,{"disambiguationData":[OSD([sQuery(id+"F0.wireOp",EDGE,"E56.bottom"),sQuery(id+"F0.wireOp",EDGE,"E56.left"),sQuery(id+"F0.wireOp",EDGE,"E91.MirrorCS"),sQuery(id+"F0.wireOp",EDGE,"E97.MirrorCS"),sQuery(id+"F0.wireOp",EDGE,"E103.MirrorCS")])],"isStart":false});
            var Q1;
            Q1=makeQuery(id+"F2.opExtrude","CAP_FACE",FACE,{"disambiguationData":[OSD([sQuery(id+"F0.wireOp",EDGE,"E56.top"),sQuery(id+"F0.wireOp",EDGE,"E56.left"),sQuery(id+"F0.wireOp",EDGE,"E84.MirrorCS"),sQuery(id+"F0.wireOp",EDGE,"E93.MirrorCS"),sQuery(id+"F0.wireOp",EDGE,"E98.MirrorCS")])],"isStart":false});
            var Q2;
            Q2=makeQuery(id+"F2.opExtrude","CAP_FACE",FACE,{"disambiguationData":[OSD([sQuery(id+"F0.wireOp",EDGE,"E56.bottom"),sQuery(id+"F0.wireOp",EDGE,"E56.right"),sQuery(id+"F0.wireOp",EDGE,"E86.MirrorCS"),sQuery(id+"F0.wireOp",EDGE,"E87.MirrorCS"),sQuery(id+"F0.wireOp",EDGE,"E94.MirrorCS")])],"isStart":false});
            var Q3;
            Q3=makeQuery(id+"F2.opExtrude","CAP_FACE",FACE,{"disambiguationData":[OSD([sQuery(id+"F0.wireOp",EDGE,"E56.top"),sQuery(id+"F0.wireOp",EDGE,"E56.right"),sQuery(id+"F0.wireOp",EDGE,"E100.MirrorCS"),sQuery(id+"F0.wireOp",EDGE,"E102.MirrorCS"),sQuery(id+"F0.wireOp",EDGE,"E104.MirrorCS")])],"isStart":false});
            var Q4;
            Q4=makeQuery(id+"F2.opExtrude","CAP_FACE",FACE,{"disambiguationData":[OSD([sQuery(id+"F0.wireOp",EDGE,"E55.top"),sQuery(id+"F0.wireOp",EDGE,"E55.left"),sQuery(id+"F0.wireOp",EDGE,"E74.MirrorCS"),sQuery(id+"F0.wireOp",EDGE,"E75.MirrorCS"),sQuery(id+"F0.wireOp",EDGE,"E76.MirrorCS")])],"isStart":false});
            var Q5;
            Q5=makeQuery(id+"F2.opExtrude","CAP_FACE",FACE,{"disambiguationData":[OSD([sQuery(id+"F0.wireOp",EDGE,"E55.bottom"),sQuery(id+"F0.wireOp",EDGE,"E55.left"),sQuery(id+"F0.wireOp",EDGE,"E71"),sQuery(id+"F0.wireOp",EDGE,"E72"),sQuery(id+"F0.wireOp",EDGE,"E73")])],"isStart":false});
            var Q6;
            Q6=makeQuery(id+"F2.opExtrude","CAP_FACE",FACE,{"disambiguationData":[OSD([sQuery(id+"F0.wireOp",EDGE,"E55.bottom"),sQuery(id+"F0.wireOp",EDGE,"E55.right"),sQuery(id+"F0.wireOp",EDGE,"E80.MirrorCS"),sQuery(id+"F0.wireOp",EDGE,"E81.MirrorCS"),sQuery(id+"F0.wireOp",EDGE,"E82.MirrorCS")])],"isStart":false});
            var Q7;
            Q7=makeQuery(id+"F2.opExtrude","CAP_FACE",FACE,{"disambiguationData":[OSD([sQuery(id+"F0.wireOp",EDGE,"E55.top"),sQuery(id+"F0.wireOp",EDGE,"E55.right"),sQuery(id+"F0.wireOp",EDGE,"E77.MirrorCS"),sQuery(id+"F0.wireOp",EDGE,"E78.MirrorCS"),sQuery(id+"F0.wireOp",EDGE,"E79.MirrorCS")])],"isStart":false});
            extrude(context, id + "F3", {"entities" : qUnion([Q0, Q1, Q2, Q3, Q4, Q5, Q6, Q7]), "operationType" : NewBodyOperationType.ADD, "oppositeDirection" : true, "depth" : 3 * mm});
        }
        {
            var Q0;
            Q0=makeQuery(id+"F0.imprint","IMPRINT",FACE,{"disambiguationData":[TD([[makeQuery(id+"F0.imprint","IMPRINT",EDGE,{"derivedFrom":sQuery(id+"F0.wireOp",EDGE,"E84.MirrorCS")}),1.0]])]});
            var Q1;
            Q1=makeQuery(id+"F0.imprint","IMPRINT",FACE,{"disambiguationData":[TD([[makeQuery(id+"F0.imprint","IMPRINT",EDGE,{"derivedFrom":sQuery(id+"F0.wireOp",EDGE,"E0")}),1.0]])]});
            var Q2;
            Q2=makeQuery(id+"F0.imprint","IMPRINT",FACE,{"disambiguationData":[TD([[makeQuery(id+"F0.imprint","IMPRINT",EDGE,{"derivedFrom":sQuery(id+"F0.wireOp",EDGE,"E86.MirrorCS")}),1.0]])]});
            var Q3;
            {var subQ0=sQuery(id+"F0.wireOp",EDGE,"E91.MirrorCS");Q3=makeQuery(id+"F0.imprint","IMPRINT",FACE,{"disambiguationData":[TD([[makeQuery(id+"F0.imprint","IMPRINT",EDGE,{"derivedFrom":subQ0}),1.0]])]});}
            var Q4;
            {var subQ3=sQuery(id+"F0.wireOp",EDGE,"E100.MirrorCS");Q4=makeQuery(id+"F0.imprint","IMPRINT",FACE,{"disambiguationData":[TD([[makeQuery(id+"F0.imprint","IMPRINT",EDGE,{"derivedFrom":subQ3}),-1.0]])]});}
            var Q5;
            Q5=makeQuery(id+"F0.imprint","IMPRINT",FACE,{"disambiguationData":[TD([[makeQuery(id+"F0.imprint","IMPRINT",EDGE,{"derivedFrom":sQuery(id+"F0.wireOp",EDGE,"E77.MirrorCS")}),1.0]])]});
            var Q6;
            {var subQ0=sQuery(id+"F0.wireOp",EDGE,"E80.MirrorCS");Q6=makeQuery(id+"F0.imprint","IMPRINT",FACE,{"disambiguationData":[TD([[makeQuery(id+"F0.imprint","IMPRINT",EDGE,{"derivedFrom":subQ0}),-1.0]])]});}
            var Q7;
            Q7=makeQuery(id+"F0.imprint","IMPRINT",FACE,{"disambiguationData":[TD([[makeQuery(id+"F0.imprint","IMPRINT",EDGE,{"derivedFrom":sQuery(id+"F0.wireOp",EDGE,"E84.MirrorCS")}),-1.0]])]});
            var Q8;
            {var subQ0=sQuery(id+"F0.wireOp",EDGE,"E74.MirrorCS");Q8=makeQuery(id+"F0.imprint","IMPRINT",FACE,{"disambiguationData":[TD([[makeQuery(id+"F0.imprint","IMPRINT",EDGE,{"derivedFrom":subQ0}),-1.0]])]});}
            var Q9;
            Q9=makeQuery(id+"F0.imprint","IMPRINT",FACE,{"disambiguationData":[TD([[makeQuery(id+"F0.imprint","IMPRINT",EDGE,{"derivedFrom":sQuery(id+"F0.wireOp",EDGE,"E71")}),1.0]])]});
            var Q10;
            Q10=makeQuery(id+"F0.imprint","IMPRINT",FACE,{"disambiguationData":[TD([[makeQuery(id+"F0.imprint","IMPRINT",EDGE,{"derivedFrom":sQuery(id+"F0.wireOp",EDGE,"E12")}),1.0]])]});
            extrude(context, id + "F4", {"entities" : qUnion([Q0, Q1, Q2, Q3, Q4, Q5, Q6, Q7, Q8, Q9, Q10]), "depth" : 55 * mm, "hasSecondDirection" : true, "secondDirectionOppositeDirection" : false, "secondDirectionDepth" : 40 * mm});
        }
        {
            var Q0;
            {var subQ0=sQuery(id+"F0.wireOp",EDGE,"E74.MirrorCS");Q0=makeQuery(id+"F0.imprint","IMPRINT",FACE,{"disambiguationData":[TD([[makeQuery(id+"F0.imprint","IMPRINT",EDGE,{"derivedFrom":subQ0}),-1.0]])]});}
            var Q1;
            Q1=makeQuery(id+"F0.imprint","IMPRINT",FACE,{"disambiguationData":[TD([[makeQuery(id+"F0.imprint","IMPRINT",EDGE,{"derivedFrom":sQuery(id+"F0.wireOp",EDGE,"E12")}),1.0]])]});
            var Q2;
            Q2=makeQuery(id+"F0.imprint","IMPRINT",FACE,{"disambiguationData":[TD([[makeQuery(id+"F0.imprint","IMPRINT",EDGE,{"derivedFrom":sQuery(id+"F0.wireOp",EDGE,"E71")}),1.0]])]});
            var Q3;
            {var subQ0=sQuery(id+"F0.wireOp",EDGE,"E80.MirrorCS");Q3=makeQuery(id+"F0.imprint","IMPRINT",FACE,{"disambiguationData":[TD([[makeQuery(id+"F0.imprint","IMPRINT",EDGE,{"derivedFrom":subQ0}),-1.0]])]});}
            var Q4;
            Q4=makeQuery(id+"F0.imprint","IMPRINT",FACE,{"disambiguationData":[TD([[makeQuery(id+"F0.imprint","IMPRINT",EDGE,{"derivedFrom":sQuery(id+"F0.wireOp",EDGE,"E77.MirrorCS")}),1.0]])]});
            var Q5;
            {var subQ0=sQuery(id+"F0.wireOp",EDGE,"E91.MirrorCS");Q5=makeQuery(id+"F0.imprint","IMPRINT",FACE,{"disambiguationData":[TD([[makeQuery(id+"F0.imprint","IMPRINT",EDGE,{"derivedFrom":subQ0}),1.0]])]});}
            var Q6;
            Q6=makeQuery(id+"F0.imprint","IMPRINT",FACE,{"disambiguationData":[TD([[makeQuery(id+"F0.imprint","IMPRINT",EDGE,{"derivedFrom":sQuery(id+"F0.wireOp",EDGE,"E84.MirrorCS")}),1.0]])]});
            var Q7;
            Q7=makeQuery(id+"F0.imprint","IMPRINT",FACE,{"disambiguationData":[TD([[makeQuery(id+"F0.imprint","IMPRINT",EDGE,{"derivedFrom":sQuery(id+"F0.wireOp",EDGE,"E84.MirrorCS")}),-1.0]])]});
            var Q8;
            {var subQ3=sQuery(id+"F0.wireOp",EDGE,"E100.MirrorCS");Q8=makeQuery(id+"F0.imprint","IMPRINT",FACE,{"disambiguationData":[TD([[makeQuery(id+"F0.imprint","IMPRINT",EDGE,{"derivedFrom":subQ3}),-1.0]])]});}
            var Q9;
            Q9=makeQuery(id+"F0.imprint","IMPRINT",FACE,{"disambiguationData":[TD([[makeQuery(id+"F0.imprint","IMPRINT",EDGE,{"derivedFrom":sQuery(id+"F0.wireOp",EDGE,"E86.MirrorCS")}),1.0]])]});
            extrude(context, id + "F5", {"entities" : qUnion([Q0, Q1, Q2, Q3, Q4, Q5, Q6, Q7, Q8, Q9]), "operationType" : NewBodyOperationType.REMOVE, "depth" : 50 * mm, "hasSecondDirection" : true, "secondDirectionOppositeDirection" : false, "secondDirectionDepth" : 40 * mm});
        }
    });
